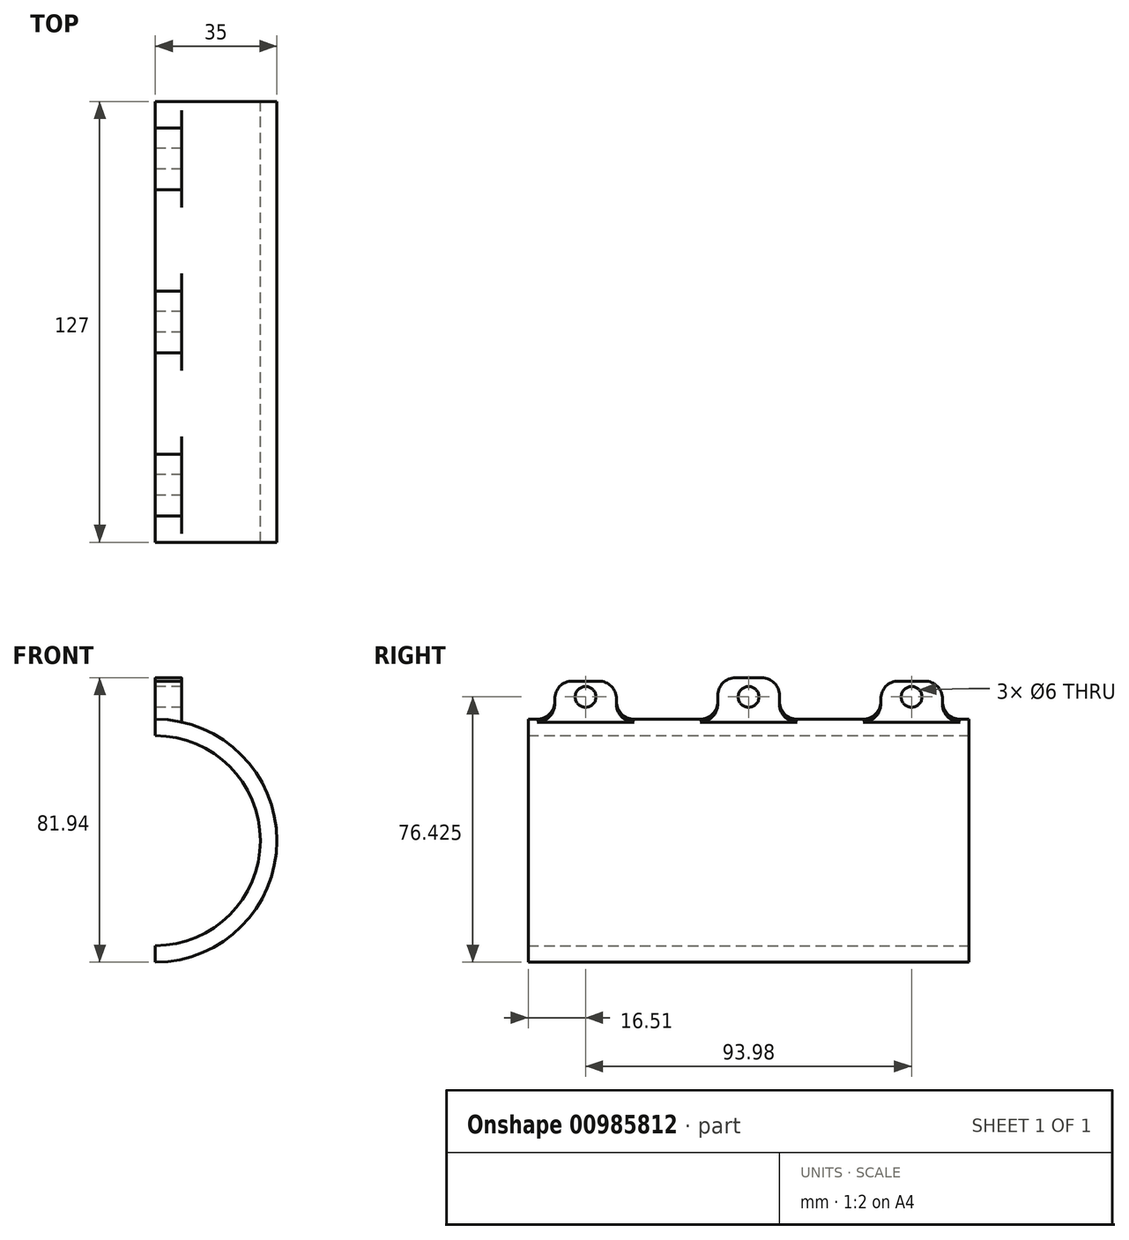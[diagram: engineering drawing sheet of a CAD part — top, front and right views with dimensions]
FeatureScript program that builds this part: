
annotation { "Feature Type Name" : "Feature", "Feature Type Description" : "" }
export const myFeature = defineFeature(function(context is Context, id is Id, definition is map)
    precondition{}
    {
        {
            var Q0;
            Q0=qCreatedBy(makeId("Front.planeOp"),FACE);
            var sketch = newSketch(context, id + "F0", { "sketchPlane" : qUnion([Q0])});
            skCircle(sketch, "E0", {"center": v(0, 0) * mm, "radius": 35 * mm});
            skCircle(sketch, "E1", {"center": v(0, 0) * mm, "radius": 30.25 * mm});
            skSolve(sketch);
        }
        {
            var Q0;
            Q0=makeQuery(id+"F0.imprint","IMPRINT",FACE,{"disambiguationData":[TD([[makeQuery(id+"F0.imprint","IMPRINT",EDGE,{"derivedFrom":sQuery(id+"F0.wireOp",EDGE,"E0")}),1.0]])]});
            extrude(context, id + "F1", {"entities" : qUnion([Q0]), "depth" : 63.5 * mm, "offsetDistance" : 25.4 * mm});
        }
        {
            var Q0;
            Q0=makeQuery(id+"F1.opExtrude","CAP_FACE",FACE,{"disambiguationData":[OSD([sQuery(id+"F0.wireOp",EDGE,"E0"),sQuery(id+"F0.wireOp",EDGE,"E1")])],"isStart":true});
            extrude(context, id + "F2", {"entities" : qUnion([Q0]), "operationType" : NewBodyOperationType.ADD, "depth" : 63.5 * mm, "offsetDistance" : 25.4 * mm});
        }
        {
            var Q0;
            Q0=qCreatedBy(makeId("Top.planeOp"),FACE);
            var sketch = newSketch(context, id + "F3", { "sketchPlane" : qUnion([Q0])});
            skLineSegment(sketch, "E2.bottom", {"start": v(0, 76.34) * mm, "end": v(-87.94, 76.34) * mm});
            skLineSegment(sketch, "E2.top", {"start": v(0, -76.81) * mm, "end": v(-87.94, -76.81) * mm});
            skLineSegment(sketch, "E2.left", {"start": v(0, 76.34) * mm, "end": v(0, -76.81) * mm});
            skLineSegment(sketch, "E2.right", {"start": v(-87.94, 76.34) * mm, "end": v(-87.94, -76.81) * mm});
            skSolve(sketch);
        }
        {
            var Q0;
            Q0=makeQuery(id+"F3.imprint","IMPRINT",FACE,{"disambiguationData":[TD([[makeQuery(id+"F3.imprint","IMPRINT",EDGE,{"derivedFrom":sQuery(id+"F3.wireOp",EDGE,"E2.bottom")}),1.0]])]});
            extrude(context, id + "F4", {"entities" : qUnion([Q0]), "operationType" : NewBodyOperationType.REMOVE, "oppositeDirection" : true, "depth" : 254 * mm, "offsetDistance" : 25.4 * mm});
        }
        {
            var Q0;
            Q0=qCreatedBy(makeId("Top.planeOp"),FACE);
            var sketch = newSketch(context, id + "F5", { "sketchPlane" : qUnion([Q0])});
            skLineSegment(sketch, "E3.bottom", {"start": v(0, 76.34) * mm, "end": v(-90.78, 76.34) * mm});
            skLineSegment(sketch, "E3.top", {"start": v(0, -70.9) * mm, "end": v(-90.78, -70.9) * mm});
            skLineSegment(sketch, "E3.left", {"start": v(0, 76.34) * mm, "end": v(0, -70.9) * mm});
            skLineSegment(sketch, "E3.right", {"start": v(-90.78, 76.34) * mm, "end": v(-90.78, -70.9) * mm});
            skSolve(sketch);
        }
        {
            var Q0;
            Q0=makeQuery(id+"F5.imprint","IMPRINT",FACE,{"disambiguationData":[TD([[makeQuery(id+"F5.imprint","IMPRINT",EDGE,{"derivedFrom":sQuery(id+"F5.wireOp",EDGE,"E3.bottom")}),1.0]])]});
            extrude(context, id + "F6", {"entities" : qUnion([Q0]), "operationType" : NewBodyOperationType.REMOVE, "depth" : 254 * mm, "offsetDistance" : 25.4 * mm});
        }
        {
            var Q0;
            Q0=qCreatedBy(makeId("Right.planeOp"),FACE);
            var sketch = newSketch(context, id + "F7", { "sketchPlane" : qUnion([Q0])});
            skLineSegment(sketch, "E4.bottom", {"start": v(-55.88, 45.97) * mm, "end": v(-38.1, 45.97) * mm});
            skLineSegment(sketch, "E4.top", {"start": v(-55.88, 30.73) * mm, "end": v(-38.1, 30.73) * mm});
            skLineSegment(sketch, "E4.left", {"start": v(-55.88, 45.97) * mm, "end": v(-55.88, 30.73) * mm});
            skLineSegment(sketch, "E4.right", {"start": v(-38.1, 45.97) * mm, "end": v(-38.1, 30.73) * mm});
            skLineSegment(sketch, "E5.bottom", {"start": v(55.88, 30.73) * mm, "end": v(38.1, 30.73) * mm});
            skLineSegment(sketch, "E5.top", {"start": v(55.88, 45.97) * mm, "end": v(38.1, 45.97) * mm});
            skLineSegment(sketch, "E5.left", {"start": v(55.88, 30.73) * mm, "end": v(55.88, 45.97) * mm});
            skLineSegment(sketch, "E5.right", {"start": v(38.1, 30.73) * mm, "end": v(38.1, 45.97) * mm});
            skPoint(sketch, "E6.centerSnap0", {"position": v(-46.99, 45.97) * mm});
            skPoint(sketch, "E6.centerSnap1", {"position": v(-55.88, 38.35) * mm});
            skPoint(sketch, "E7.centerSnap0", {"position": v(46.99, 45.97) * mm});
            skCircle(sketch, "E8", {"center": v(46.99, 41.43) * mm, "radius": 3 * mm});
            skCircle(sketch, "E9", {"center": v(-46.99, 41.43) * mm, "radius": 3 * mm});
            skLineSegment(sketch, "E10.bottom", {"start": v(0, 30.73) * mm, "end": v(-8.89, 30.73) * mm});
            skLineSegment(sketch, "E10.top", {"start": v(0, 46.94) * mm, "end": v(-8.9, 46.94) * mm});
            skLineSegment(sketch, "E10.right", {"start": v(-8.89, 30.73) * mm, "end": v(-8.9, 46.94) * mm});
            skLineSegment(sketch, "E11.bottom", {"start": v(0, 46.94) * mm, "end": v(8.89, 46.94) * mm});
            skLineSegment(sketch, "E11.top", {"start": v(0, 30.73) * mm, "end": v(8.89, 30.73) * mm});
            skLineSegment(sketch, "E11.right", {"start": v(8.89, 46.94) * mm, "end": v(8.89, 30.73) * mm});
            skCircle(sketch, "E12", {"center": v(0, 41.43) * mm, "radius": 3 * mm});
            skSolve(sketch);
        }
        {
            var Q0;
            Q0=makeQuery(id+"F7.imprint","IMPRINT",FACE,{"disambiguationData":[TD([[makeQuery(id+"F7.imprint","IMPRINT",EDGE,{"derivedFrom":sQuery(id+"F7.wireOp",EDGE,"E4.bottom")}),-1.0]])]});
            var Q1;
            Q1=makeQuery(id+"F7.imprint","IMPRINT",FACE,{"disambiguationData":[TD([[makeQuery(id+"F7.imprint","IMPRINT",EDGE,{"derivedFrom":sQuery(id+"F7.wireOp",EDGE,"E10.bottom")}),-1.0]])]});
            var Q2;
            Q2=makeQuery(id+"F7.imprint","IMPRINT",FACE,{"disambiguationData":[TD([[makeQuery(id+"F7.imprint","IMPRINT",EDGE,{"derivedFrom":sQuery(id+"F7.wireOp",EDGE,"E5.bottom")}),-1.0]])]});
            extrude(context, id + "F8", {"entities" : qUnion([Q0, Q1, Q2]), "operationType" : NewBodyOperationType.ADD, "depth" : 7.62 * mm, "offsetDistance" : 25.4 * mm});
        }
        {
            var Q0;
            Q0=makeQuery(id+"F8.opExtrude","SWEPT_EDGE",EDGE,{"disambiguationData":[OSD([sQuery(id+"F7.wireOp",EDGE,"E4.bottom"),sQuery(id+"F7.wireOp",EDGE,"E4.left")])]});
            var Q1;
            Q1=makeQuery(id+"F8.opExtrude","SWEPT_EDGE",EDGE,{"disambiguationData":[OSD([sQuery(id+"F7.wireOp",EDGE,"E4.bottom"),sQuery(id+"F7.wireOp",EDGE,"E4.right")])]});
            var Q2;
            Q2=makeQuery(id+"F8.opExtrude","SWEPT_EDGE",EDGE,{"disambiguationData":[OSD([sQuery(id+"F7.wireOp",EDGE,"E10.top"),sQuery(id+"F7.wireOp",EDGE,"E10.right")])]});
            var Q3;
            Q3=makeQuery(id+"F8.opExtrude","SWEPT_EDGE",EDGE,{"disambiguationData":[OSD([sQuery(id+"F7.wireOp",EDGE,"E11.bottom"),sQuery(id+"F7.wireOp",EDGE,"E11.right")])]});
            var Q4;
            Q4=makeQuery(id+"F8.opExtrude","SWEPT_EDGE",EDGE,{"disambiguationData":[OSD([sQuery(id+"F7.wireOp",EDGE,"E5.top"),sQuery(id+"F7.wireOp",EDGE,"E5.right")])]});
            var Q5;
            Q5=makeQuery(id+"F8.opExtrude","SWEPT_EDGE",EDGE,{"disambiguationData":[OSD([sQuery(id+"F7.wireOp",EDGE,"E5.top"),sQuery(id+"F7.wireOp",EDGE,"E5.left")])]});
            var Q6;
            {var subQ0=sQuery(id+"F0.wireOp",EDGE,"E0");Q6=makeQuery(id+"F8.boolean.opBoolean","INTERSECT",EDGE,{"derivedFrom":[makeQuery(id+"F2.boolean.opBoolean","MERGE",FACE,{"derivedFrom":[makeQuery(id+"F1.opExtrude","SWEPT_FACE",FACE,{"disambiguationData":[OSD([subQ0])]}),makeQuery(id+"F2.opExtrude","SWEPT_FACE",FACE,{"disambiguationData":[OSD([subQ0])]})]}),makeQuery(id+"F8.opExtrude","SWEPT_FACE",FACE,{"disambiguationData":[OSD([sQuery(id+"F7.wireOp",EDGE,"E4.right")])]})]});}
            var Q7;
            {var subQ0=sQuery(id+"F0.wireOp",EDGE,"E0");Q7=makeQuery(id+"F8.boolean.opBoolean","INTERSECT",EDGE,{"derivedFrom":[makeQuery(id+"F2.boolean.opBoolean","MERGE",FACE,{"derivedFrom":[makeQuery(id+"F1.opExtrude","SWEPT_FACE",FACE,{"disambiguationData":[OSD([subQ0])]}),makeQuery(id+"F2.opExtrude","SWEPT_FACE",FACE,{"disambiguationData":[OSD([subQ0])]})]}),makeQuery(id+"F8.opExtrude","SWEPT_FACE",FACE,{"disambiguationData":[OSD([sQuery(id+"F7.wireOp",EDGE,"E11.right")])]})]});}
            var Q8;
            {var subQ0=sQuery(id+"F0.wireOp",EDGE,"E0");Q8=makeQuery(id+"F8.boolean.opBoolean","INTERSECT",EDGE,{"derivedFrom":[makeQuery(id+"F2.boolean.opBoolean","MERGE",FACE,{"derivedFrom":[makeQuery(id+"F1.opExtrude","SWEPT_FACE",FACE,{"disambiguationData":[OSD([subQ0])]}),makeQuery(id+"F2.opExtrude","SWEPT_FACE",FACE,{"disambiguationData":[OSD([subQ0])]})]}),makeQuery(id+"F8.opExtrude","SWEPT_FACE",FACE,{"disambiguationData":[OSD([sQuery(id+"F7.wireOp",EDGE,"E5.right")])]})]});}
            var Q9;
            {var subQ0=sQuery(id+"F0.wireOp",EDGE,"E0");Q9=makeQuery(id+"F8.boolean.opBoolean","INTERSECT",EDGE,{"derivedFrom":[makeQuery(id+"F2.boolean.opBoolean","MERGE",FACE,{"derivedFrom":[makeQuery(id+"F1.opExtrude","SWEPT_FACE",FACE,{"disambiguationData":[OSD([subQ0])]}),makeQuery(id+"F2.opExtrude","SWEPT_FACE",FACE,{"disambiguationData":[OSD([subQ0])]})]}),makeQuery(id+"F8.opExtrude","SWEPT_FACE",FACE,{"disambiguationData":[OSD([sQuery(id+"F7.wireOp",EDGE,"E10.right")])]})]});}
            var Q10;
            {var subQ0=sQuery(id+"F0.wireOp",EDGE,"E0");Q10=makeQuery(id+"F8.boolean.opBoolean","INTERSECT",EDGE,{"derivedFrom":[makeQuery(id+"F2.boolean.opBoolean","MERGE",FACE,{"derivedFrom":[makeQuery(id+"F1.opExtrude","SWEPT_FACE",FACE,{"disambiguationData":[OSD([subQ0])]}),makeQuery(id+"F2.opExtrude","SWEPT_FACE",FACE,{"disambiguationData":[OSD([subQ0])]})]}),makeQuery(id+"F8.opExtrude","SWEPT_FACE",FACE,{"disambiguationData":[OSD([sQuery(id+"F7.wireOp",EDGE,"E4.left")])]})]});}
            var Q11;
            {var subQ0=sQuery(id+"F0.wireOp",EDGE,"E0");Q11=makeQuery(id+"F8.boolean.opBoolean","INTERSECT",EDGE,{"derivedFrom":[makeQuery(id+"F2.boolean.opBoolean","MERGE",FACE,{"derivedFrom":[makeQuery(id+"F1.opExtrude","SWEPT_FACE",FACE,{"disambiguationData":[OSD([subQ0])]}),makeQuery(id+"F2.opExtrude","SWEPT_FACE",FACE,{"disambiguationData":[OSD([subQ0])]})]}),makeQuery(id+"F8.opExtrude","SWEPT_FACE",FACE,{"disambiguationData":[OSD([sQuery(id+"F7.wireOp",EDGE,"E5.left")])]})]});}
            fillet(context, id + "F9", {"entities" : qUnion([Q0, Q1, Q2, Q3, Q4, Q5, Q6, Q7, Q8, Q9, Q10, Q11]), "radius" : 5.08 * mm, "tangentPropagation" : true, "allowEdgeOverflow" : false});
        }
    });
